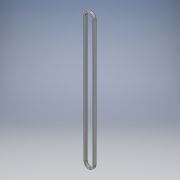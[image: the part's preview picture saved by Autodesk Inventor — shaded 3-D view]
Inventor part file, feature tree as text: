
AUTODESK INVENTOR PART (.ipt)
format: ipt  version: 2016 (Build 200138000, 138)  size: 115,712 bytes
history: native  units: in
note: dims shown in document units (in); Inventor stores cm internally (conversion verified against a paired STEP export)
features: fillet x4, shell x2, extrude x1, sketch x1
ambient origin geometry x8: Origin, YZ Plane, XZ Plane, XY Plane, X Axis, Y Axis, Z Axis, Center Point
bodies: Solid1 (feature_tree)
feature tree (8):
  extrude  "Extrusion1"  Depth=0.25in TaperAngle=0.0deg
  fillet  "Fillet1"  Radius=0.5in
  fillet  "Fillet2"  Radius=0.5in
  fillet  "Fillet3"  Radius=0.5in
  fillet  "Fillet4"  Radius=0.5in
  shell  "Shell1"  Thickness=0.1in
  shell  "Shell2"  Thickness=0.1in
  sketch  "Sketch1"  dims[d0=14.0in d1=0.25in d2=0.0in d3=0.5in d4=0.5in d5=0.5in d6=0.5in d7=0.1in d8=0.1in]
